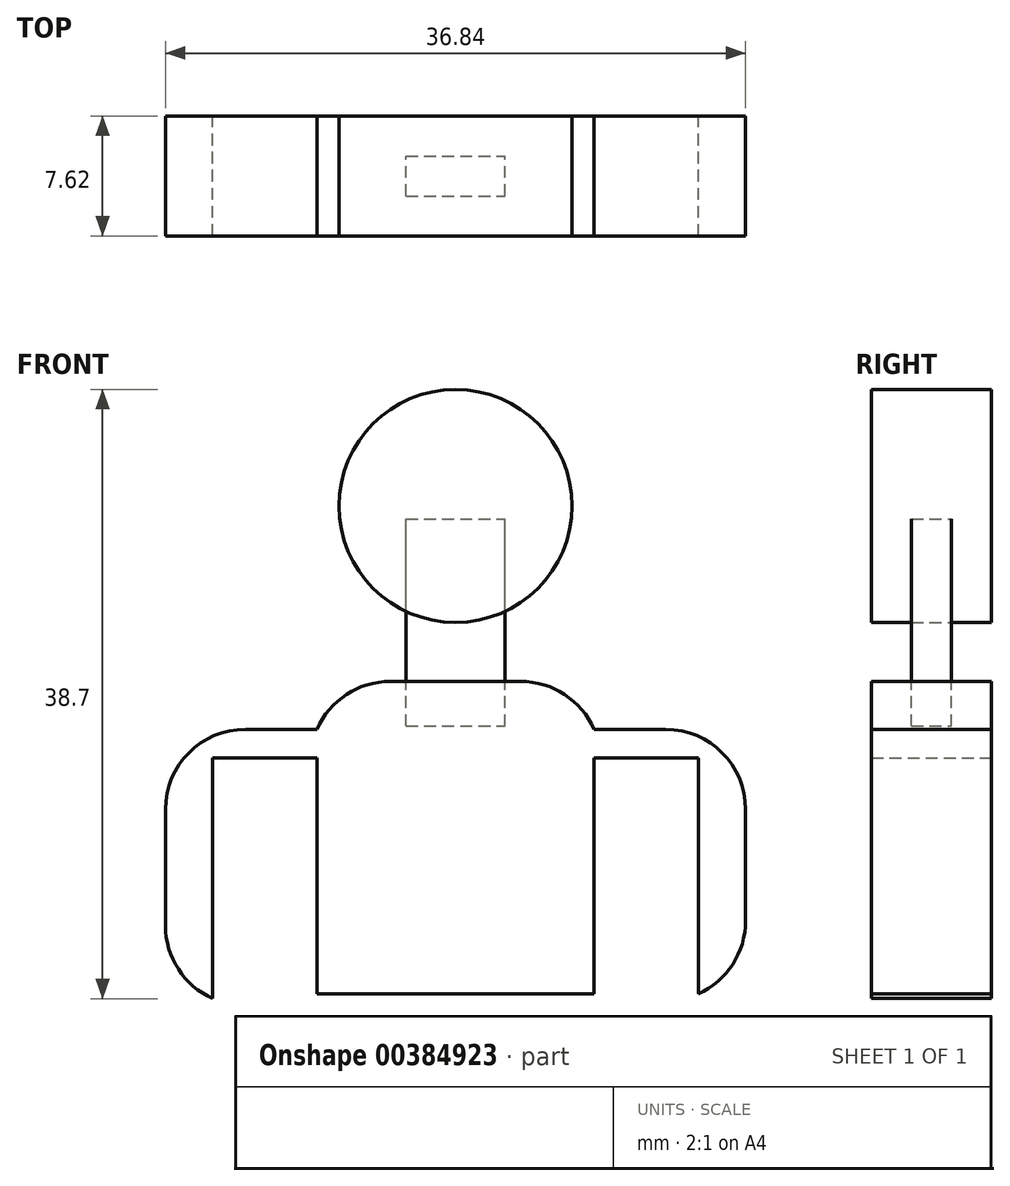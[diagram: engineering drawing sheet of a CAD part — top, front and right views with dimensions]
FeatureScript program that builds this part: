
annotation { "Feature Type Name" : "Feature", "Feature Type Description" : "" }
export const myFeature = defineFeature(function(context is Context, id is Id, definition is map)
    precondition{}
    {
        {
            var Q0;
            Q0=qCreatedBy(makeId("Front.planeOp"),FACE);
            var sketch = newSketch(context, id + "F0", { "sketchPlane" : qUnion([Q0])});
            skCircle(sketch, "E0", {"center": v(0, 40.9) * mm, "radius": 7.4 * mm});
            skLineSegment(sketch, "E1.bottom", {"start": v(-3.14, 26.92) * mm, "end": v(3.14, 26.92) * mm});
            skLineSegment(sketch, "E1.top", {"start": v(-3.14, 40.1) * mm, "end": v(3.14, 40.1) * mm});
            skLineSegment(sketch, "E1.left", {"start": v(-3.14, 26.92) * mm, "end": v(-3.14, 40.1) * mm});
            skLineSegment(sketch, "E1.right", {"start": v(3.14, 26.92) * mm, "end": v(3.14, 40.1) * mm});
            skPoint(sketch, "E1.middle", {"position": v(0, 33.5) * mm});
            skLineSegment(sketch, "E2.bottom", {"start": v(-8.8, 9.92) * mm, "end": v(8.8, 9.92) * mm});
            skLineSegment(sketch, "E2.top", {"start": v(-8.8, 29.76) * mm, "end": v(8.8, 29.76) * mm});
            skLineSegment(sketch, "E2.left", {"start": v(-8.8, 9.92) * mm, "end": v(-8.8, 29.76) * mm});
            skLineSegment(sketch, "E2.right", {"start": v(8.8, 9.92) * mm, "end": v(8.8, 29.76) * mm});
            skPoint(sketch, "E2.middle", {"position": v(0, 19.84) * mm});
            skLineSegment(sketch, "E3.bottom", {"start": v(8.8, 26.72) * mm, "end": v(15.41, 26.72) * mm});
            skLineSegment(sketch, "E3.top", {"start": v(8.8, 24.91) * mm, "end": v(15.41, 24.91) * mm});
            skLineSegment(sketch, "E3.left", {"start": v(8.8, 26.72) * mm, "end": v(8.8, 24.91) * mm});
            skLineSegment(sketch, "E3.right", {"start": v(15.41, 26.72) * mm, "end": v(15.41, 24.91) * mm});
            skLineSegment(sketch, "E4.bottom", {"start": v(-8.8, 26.72) * mm, "end": v(-15.41, 26.72) * mm});
            skLineSegment(sketch, "E4.top", {"start": v(-8.8, 24.91) * mm, "end": v(-15.41, 24.91) * mm});
            skLineSegment(sketch, "E4.left", {"start": v(-8.8, 26.72) * mm, "end": v(-8.8, 24.91) * mm});
            skLineSegment(sketch, "E4.right", {"start": v(-15.41, 26.72) * mm, "end": v(-15.41, 24.91) * mm});
            skLineSegment(sketch, "E5.bottom", {"start": v(8.8, 9.92) * mm, "end": v(3.14, 9.92) * mm});
            skLineSegment(sketch, "E5.top", {"start": v(8.8, -6.03) * mm, "end": v(3.14, -6.03) * mm});
            skLineSegment(sketch, "E5.left", {"start": v(8.8, 9.92) * mm, "end": v(8.8, -6.03) * mm});
            skLineSegment(sketch, "E5.right", {"start": v(3.14, 9.92) * mm, "end": v(3.14, -6.03) * mm});
            skLineSegment(sketch, "E6.bottom", {"start": v(-8.8, 9.92) * mm, "end": v(-2.78, 9.92) * mm});
            skLineSegment(sketch, "E6.top", {"start": v(-8.8, -6.03) * mm, "end": v(-2.78, -6.03) * mm});
            skLineSegment(sketch, "E6.left", {"start": v(-8.8, 9.92) * mm, "end": v(-8.8, -6.03) * mm});
            skLineSegment(sketch, "E6.right", {"start": v(-2.78, 9.92) * mm, "end": v(-2.78, -6.03) * mm});
            skLineSegment(sketch, "E7.bottom", {"start": v(-15.41, 26.72) * mm, "end": v(-18.42, 26.72) * mm});
            skLineSegment(sketch, "E7.top", {"start": v(-15.41, 9.61) * mm, "end": v(-18.42, 9.61) * mm});
            skLineSegment(sketch, "E7.left", {"start": v(-15.41, 26.72) * mm, "end": v(-15.41, 9.61) * mm});
            skLineSegment(sketch, "E7.right", {"start": v(-18.42, 26.72) * mm, "end": v(-18.42, 9.61) * mm});
            skLineSegment(sketch, "E8.bottom", {"start": v(15.41, 26.72) * mm, "end": v(18.42, 26.72) * mm});
            skLineSegment(sketch, "E8.top", {"start": v(15.41, 9.92) * mm, "end": v(18.42, 9.92) * mm});
            skLineSegment(sketch, "E8.left", {"start": v(15.41, 26.72) * mm, "end": v(15.41, 9.92) * mm});
            skLineSegment(sketch, "E8.right", {"start": v(18.42, 26.72) * mm, "end": v(18.42, 9.92) * mm});
            skSolve(sketch);
        }
        {
            var Q0;
            {var subQ13=sQuery(id+"F0.wireOp",EDGE,"E1.bottom");Q0=makeQuery(id+"F0.imprint","IMPRINT",FACE,{"disambiguationData":[TD([[makeQuery(id+"F0.imprint","IMPRINT",EDGE,{"derivedFrom":subQ13}),-1.0]])]});}
            var Q1;
            Q1=makeQuery(id+"F0.imprint","IMPRINT",FACE,{"disambiguationData":[TD([[makeQuery(id+"F0.imprint","IMPRINT",EDGE,{"derivedFrom":sQuery(id+"F0.wireOp",EDGE,"E6.bottom")}),-1.0]])]});
            var Q2;
            {var subQ3=sQuery(id+"F0.wireOp",EDGE,"E7.bottom");Q2=makeQuery(id+"F0.imprint","IMPRINT",FACE,{"disambiguationData":[TD([[makeQuery(id+"F0.imprint","IMPRINT",EDGE,{"derivedFrom":subQ3}),1.0]])]});}
            var Q3;
            {var subQ0=sQuery(id+"F0.wireOp",EDGE,"E4.bottom");Q3=makeQuery(id+"F0.imprint","IMPRINT",FACE,{"disambiguationData":[TD([[makeQuery(id+"F0.imprint","IMPRINT",EDGE,{"derivedFrom":subQ0}),1.0]])]});}
            var Q4;
            {var subQ3=sQuery(id+"F0.wireOp",EDGE,"E8.bottom");Q4=makeQuery(id+"F0.imprint","IMPRINT",FACE,{"disambiguationData":[TD([[makeQuery(id+"F0.imprint","IMPRINT",EDGE,{"derivedFrom":subQ3}),-1.0]])]});}
            var Q5;
            {var subQ0=sQuery(id+"F0.wireOp",EDGE,"E3.bottom");Q5=makeQuery(id+"F0.imprint","IMPRINT",FACE,{"disambiguationData":[TD([[makeQuery(id+"F0.imprint","IMPRINT",EDGE,{"derivedFrom":subQ0}),-1.0]])]});}
            var Q6;
            Q6=makeQuery(id+"F0.imprint","IMPRINT",FACE,{"disambiguationData":[TD([[makeQuery(id+"F0.imprint","IMPRINT",EDGE,{"derivedFrom":sQuery(id+"F0.wireOp",EDGE,"E5.bottom")}),1.0]])]});
            var Q7;
            {var subQ5=sQuery(id+"F0.wireOp",EDGE,"E1.top");Q7=makeQuery(id+"F0.imprint","IMPRINT",FACE,{"disambiguationData":[TD([[makeQuery(id+"F0.imprint","IMPRINT",EDGE,{"derivedFrom":subQ5}),1.0]])]});}
            var Q8;
            {var subQ5=sQuery(id+"F0.wireOp",EDGE,"E1.top");Q8=makeQuery(id+"F0.imprint","IMPRINT",FACE,{"disambiguationData":[TD([[makeQuery(id+"F0.imprint","IMPRINT",EDGE,{"derivedFrom":subQ5}),-1.0]])]});}
            var Q9;
            {var subQ0=sQuery(id+"F0.wireOp",EDGE,"E1.bottom");Q9=makeQuery(id+"F0.imprint","IMPRINT",FACE,{"disambiguationData":[TD([[makeQuery(id+"F0.imprint","IMPRINT",EDGE,{"derivedFrom":subQ0}),1.0]])]});}
            extrude(context, id + "F1", {"entities" : qUnion([Q0, Q1, Q2, Q3, Q4, Q5, Q6, Q7, Q8, Q9]), "endBound" : BoundingType.SYMMETRIC, "depth" : 7.62 * mm});
        }
        {
            var Q0;
            {var subQ0=sQuery(id+"F0.wireOp",EDGE,"E1.bottom");Q0=makeQuery(id+"F0.imprint","IMPRINT",FACE,{"disambiguationData":[TD([[makeQuery(id+"F0.imprint","IMPRINT",EDGE,{"derivedFrom":subQ0}),1.0]])]});}
            var Q1;
            {var subQ0=sQuery(id+"F0.wireOp",EDGE,"E1.left");var subQ1=sQuery(id+"F0.wireOp",EDGE,"E0");var subQ2=makeQuery(id+"F0.imprint","INTERSECT",VERTEX,{"derivedFrom":[subQ1,subQ0]});Q1=makeQuery(id+"F0.imprint","IMPRINT",FACE,{"disambiguationData":[TD([[makeQuery(id+"F0.imprint","IMPRINT",EDGE,{"disambiguationData":[TD([[subQ2,-1.0]])],"derivedFrom":subQ1}),-1.0]])]});}
            var Q2;
            {var subQ5=sQuery(id+"F0.wireOp",EDGE,"E1.top");Q2=makeQuery(id+"F0.imprint","IMPRINT",FACE,{"disambiguationData":[TD([[makeQuery(id+"F0.imprint","IMPRINT",EDGE,{"derivedFrom":subQ5}),-1.0]])]});}
            extrude(context, id + "F2", {"entities" : qUnion([Q0, Q1, Q2]), "endBound" : BoundingType.SYMMETRIC, "depth" : 2.54 * mm});
        }
        {
            var Q0;
            Q0=makeQuery(id+"F1.opExtrude","SWEPT_EDGE",EDGE,{"disambiguationData":[OSD([sQuery(id+"F0.wireOp",EDGE,"E7.bottom"),sQuery(id+"F0.wireOp",EDGE,"E7.right")])]});
            var Q1;
            Q1=makeQuery(id+"F1.opExtrude","SWEPT_EDGE",EDGE,{"disambiguationData":[OSD([sQuery(id+"F0.wireOp",EDGE,"E8.bottom"),sQuery(id+"F0.wireOp",EDGE,"E8.right")])]});
            fillet(context, id + "F3", {"entities" : qUnion([Q0, Q1]), "radius" : 5.08 * mm, "tangentPropagation" : true, "allowEdgeOverflow" : false});
        }
        {
            var Q0;
            Q0=makeQuery(id+"F1.opExtrude","SWEPT_EDGE",EDGE,{"disambiguationData":[OSD([sQuery(id+"F0.wireOp",EDGE,"E8.top"),sQuery(id+"F0.wireOp",EDGE,"E8.right")])]});
            var Q1;
            Q1=makeQuery(id+"F1.opExtrude","SWEPT_EDGE",EDGE,{"disambiguationData":[OSD([sQuery(id+"F0.wireOp",EDGE,"E7.top"),sQuery(id+"F0.wireOp",EDGE,"E7.right")])]});
            fillet(context, id + "F4", {"entities" : qUnion([Q0, Q1]), "radius" : 5.08 * mm, "tangentPropagation" : true, "allowEdgeOverflow" : false});
        }
        {
            var Q0;
            Q0=makeQuery(id+"F1.opExtrude","SWEPT_EDGE",EDGE,{"disambiguationData":[OSD([sQuery(id+"F0.wireOp",EDGE,"E2.top"),sQuery(id+"F0.wireOp",EDGE,"E2.right")])]});
            var Q1;
            Q1=makeQuery(id+"F1.opExtrude","SWEPT_EDGE",EDGE,{"disambiguationData":[OSD([sQuery(id+"F0.wireOp",EDGE,"E2.top"),sQuery(id+"F0.wireOp",EDGE,"E2.left")])]});
            fillet(context, id + "F5", {"entities" : qUnion([Q0, Q1]), "radius" : 5.08 * mm, "tangentPropagation" : true, "allowEdgeOverflow" : false});
        }
    });
